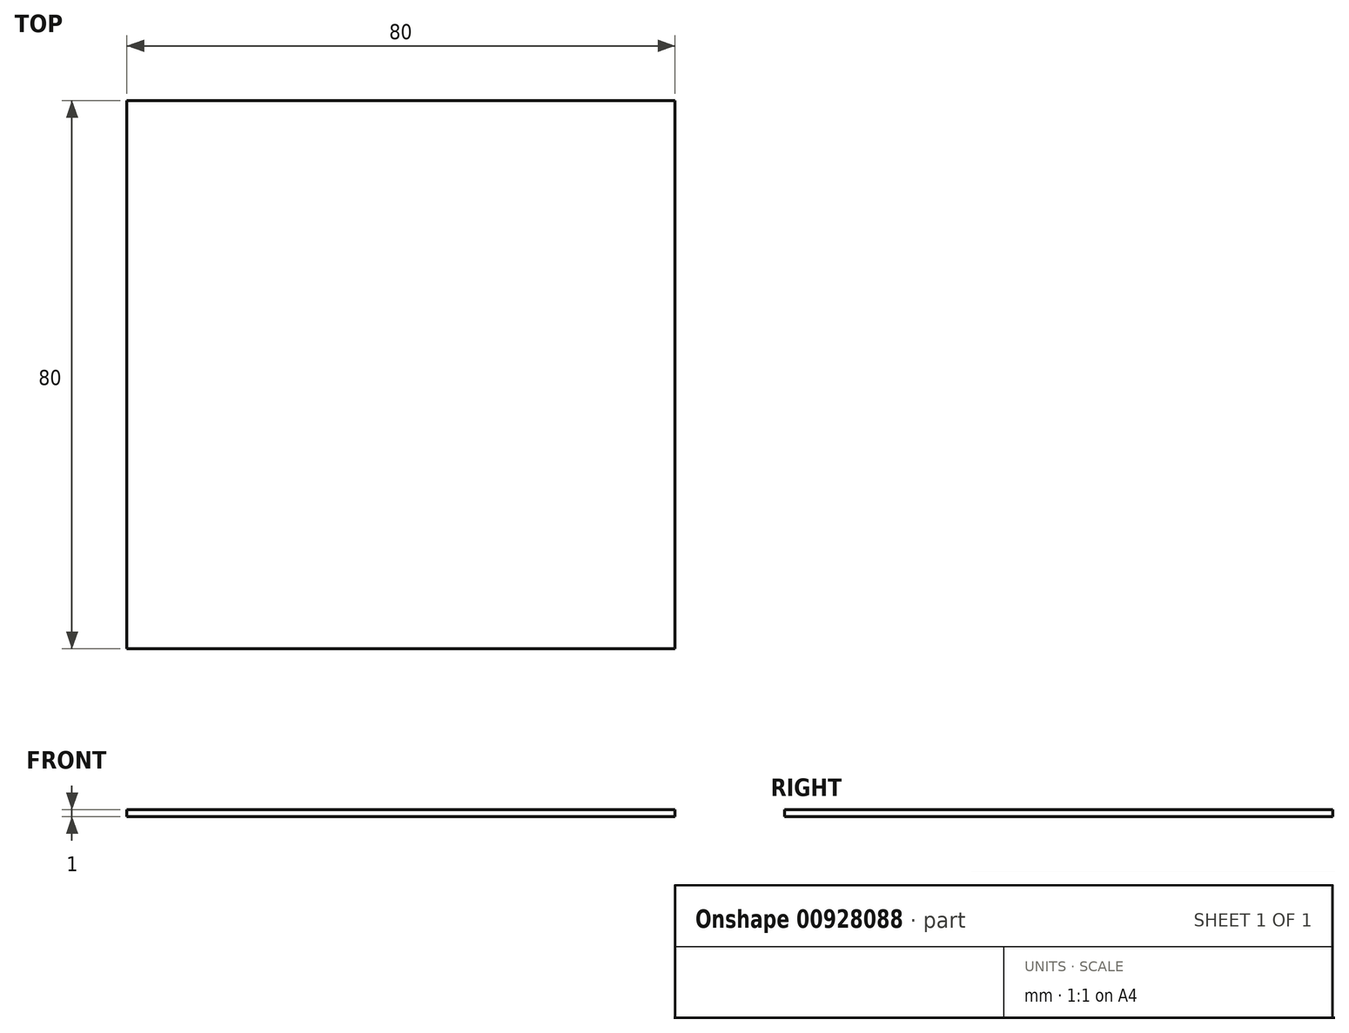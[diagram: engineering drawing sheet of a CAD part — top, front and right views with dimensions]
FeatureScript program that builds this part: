
annotation { "Feature Type Name" : "Feature", "Feature Type Description" : "" }
export const myFeature = defineFeature(function(context is Context, id is Id, definition is map)
    precondition{}
    {
        {
            var Q0;
            Q0=qCreatedBy(makeId("Top.planeOp"),FACE);
            var sketch = newSketch(context, id + "F0", { "sketchPlane" : qUnion([Q0])});
            skLineSegment(sketch, "E0.bottom", {"start": v(-40, 40) * mm, "end": v(40, 40) * mm});
            skLineSegment(sketch, "E0.top", {"start": v(-40, -40) * mm, "end": v(40, -40) * mm});
            skLineSegment(sketch, "E0.left", {"start": v(-40, 40) * mm, "end": v(-40, -40) * mm});
            skLineSegment(sketch, "E0.right", {"start": v(40, 40) * mm, "end": v(40, -40) * mm});
            skPoint(sketch, "E0.middle", {"position": v(0, 0) * mm});
            skSolve(sketch);
        }
        {
            var Q0;
            Q0=makeQuery(id+"F0.imprint","IMPRINT",FACE,{"disambiguationData":[TD([[makeQuery(id+"F0.imprint","IMPRINT",EDGE,{"derivedFrom":sQuery(id+"F0.wireOp",EDGE,"E0.bottom")}),-1.0]])]});
            extrude(context, id + "F1", {"entities" : qUnion([Q0]), "depth" : 1 * mm, "offsetDistance" : 25 * mm});
        }
    });
